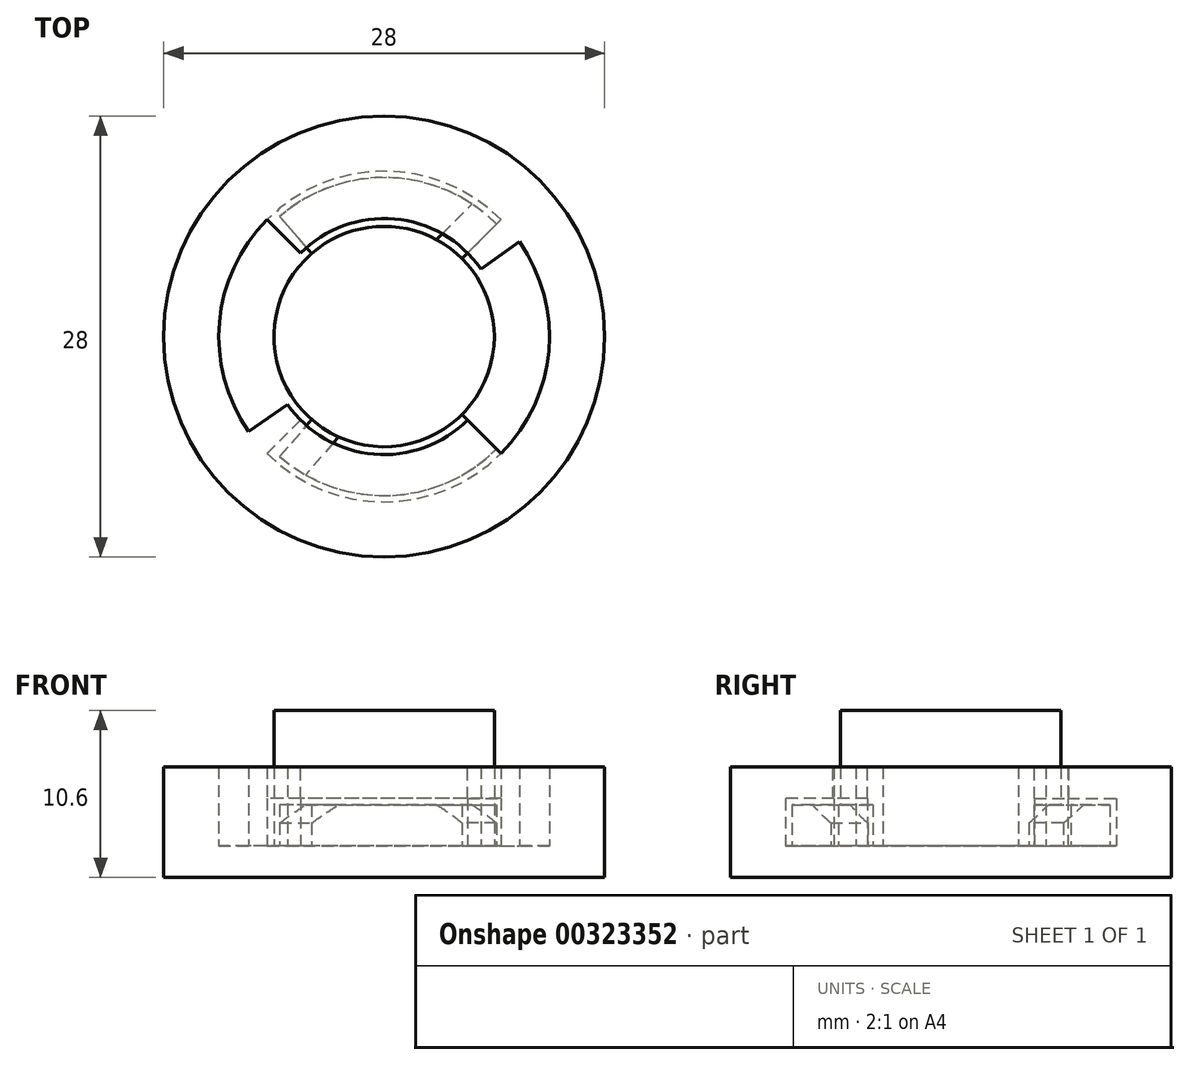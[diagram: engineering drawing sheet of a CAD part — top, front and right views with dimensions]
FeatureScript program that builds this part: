
annotation { "Feature Type Name" : "Feature", "Feature Type Description" : "" }
export const myFeature = defineFeature(function(context is Context, id is Id, definition is map)
    precondition{}
    {
        {
            var Q0;
            Q0=qCreatedBy(makeId("Top.planeOp"),FACE);
            var sketch = newSketch(context, id + "F0", { "sketchPlane" : qUnion([Q0])});
            skCircle(sketch, "E0", {"center": v(0, 0) * mm, "radius": 14 * mm});
            skSolve(sketch);
        }
        {
            var Q0;
            Q0 = qSketchRegion(id + "F0", true);
            extrude(context, id + "F1", {"entities" : qUnion([Q0]), "depth" : 2 * mm, "offsetDistance" : 25 * mm});
        }
        {
            var Q0;
            Q0=makeQuery(id+"F1.opExtrude","CAP_FACE",FACE,{"disambiguationData":[OSD([sQuery(id+"F0.wireOp",EDGE,"E0")])],"isStart":false});
            var sketch = newSketch(context, id + "F2", { "sketchPlane" : qUnion([Q0])});
            skCircle(sketch, "E1", {"center": v(0, 0) * mm, "radius": 14 * mm});
            skCircle(sketch, "E2", {"center": v(0, 0) * mm, "radius": 10.5 * mm});
            skSolve(sketch);
        }
        {
            var Q0;
            Q0 = qSketchRegion(id + "F2", true);
            extrude(context, id + "F3", {"entities" : qUnion([Q0]), "operationType" : NewBodyOperationType.ADD, "depth" : 5 * mm, "offsetDistance" : 25 * mm});
        }
        {
            var Q0;
            Q0=makeQuery(id+"F3.opExtrude","CAP_FACE",FACE,{"disambiguationData":[OSD([sQuery(id+"F2.wireOp",EDGE,"E1"),sQuery(id+"F2.wireOp",EDGE,"E2")])],"isStart":false});
            var sketch = newSketch(context, id + "F4", { "sketchPlane" : qUnion([Q0])});
            skArc(sketch, "E3", {"start": v(-9.9, 9.9) * mm, "mid": v(0, 14) * mm, "end": v(9.9, 9.9) * mm});
            skLineSegment(sketch, "E4", {"start": v(-5.3, 5.3) * mm, "end": v(-9.9, 9.9) * mm});
            skLineSegment(sketch, "E5", {"start": v(5.3, 5.3) * mm, "end": v(9.9, 9.9) * mm});
            skArc(sketch, "E6", {"start": v(-5.3, 5.3) * mm, "mid": v(0, 7.5) * mm, "end": v(5.3, 5.3) * mm});
            skLineSegment(sketch, "E7.MirrorCS", {"start": v(-5.3, -5.3) * mm, "end": v(-9.9, -9.9) * mm});
            skLineSegment(sketch, "E8.MirrorCS", {"start": v(5.3, -5.3) * mm, "end": v(9.9, -9.9) * mm});
            skArc(sketch, "E9.MirrorCS", {"start": v(-5.3, -5.3) * mm, "mid": v(0, -7.5) * mm, "end": v(5.3, -5.3) * mm});
            skArc(sketch, "E10.MirrorCS", {"start": v(-9.9, -9.9) * mm, "mid": v(0, -14) * mm, "end": v(9.9, -9.9) * mm});
            skSolve(sketch);
        }
        {
            var Q0;
            Q0 = qSketchRegion(id + "F4", true);
            extrude(context, id + "F5", {"entities" : qUnion([Q0]), "operationType" : NewBodyOperationType.ADD, "oppositeDirection" : true, "depth" : 2 * mm, "offsetDistance" : 25 * mm});
        }
        {
            var Q0;
            Q0=makeQuery(id+"F1.opExtrude","CAP_FACE",FACE,{"disambiguationData":[OSD([sQuery(id+"F0.wireOp",EDGE,"E0")])],"isStart":false});
            var sketch = newSketch(context, id + "F6", { "sketchPlane" : qUnion([Q0])});
            skLineSegment(sketch, "E11", {"start": v(-11.88, 14.16) * mm, "end": v(11.75, -14) * mm, "construction": true});
            skArc(sketch, "E12", {"start": v(7.42, 7.42) * mm, "mid": v(8.04, 6.75) * mm, "end": v(8.6, 6.02) * mm});
            skArc(sketch, "E13", {"start": v(5.3, 5.3) * mm, "mid": v(5.75, 4.82) * mm, "end": v(6.14, 4.3) * mm});
            skLineSegment(sketch, "E14", {"start": v(6.14, 4.3) * mm, "end": v(8.6, 6.02) * mm});
            skLineSegment(sketch, "E15", {"start": v(5.3, 5.3) * mm, "end": v(7.42, 7.42) * mm});
            skArc(sketch, "E16.MirrorCS", {"start": v(-6.14, -4.3) * mm, "mid": v(-5.75, -4.82) * mm, "end": v(-5.3, -5.3) * mm});
            skArc(sketch, "E17.MirrorCS", {"start": v(-8.6, -6.02) * mm, "mid": v(-8.04, -6.75) * mm, "end": v(-7.42, -7.42) * mm});
            skLineSegment(sketch, "E18.MirrorCS", {"start": v(-5.3, -5.3) * mm, "end": v(-7.42, -7.42) * mm});
            skLineSegment(sketch, "E19.MirrorCS", {"start": v(-6.14, -4.3) * mm, "end": v(-8.6, -6.02) * mm});
            skSolve(sketch);
        }
        {
            var Q0;
            Q0 = qSketchRegion(id + "F6", true);
            var Q1;
            Q1=makeQuery(id+"F5.boolean.opBoolean","MERGE",FACE,{"derivedFrom":[makeQuery(id+"F3.opExtrude","CAP_FACE",FACE,{"disambiguationData":[OSD([sQuery(id+"F2.wireOp",EDGE,"E1"),sQuery(id+"F2.wireOp",EDGE,"E2")])],"isStart":false}),makeQuery(id+"F5.opExtrude","CAP_FACE",FACE,{"disambiguationData":[OSD([sQuery(id+"F4.wireOp",EDGE,"E3"),sQuery(id+"F4.wireOp",EDGE,"E4"),sQuery(id+"F4.wireOp",EDGE,"E5"),sQuery(id+"F4.wireOp",EDGE,"E6")])],"isStart":true}),makeQuery(id+"F5.opExtrude","CAP_FACE",FACE,{"disambiguationData":[OSD([sQuery(id+"F4.wireOp",EDGE,"E7.MirrorCS"),sQuery(id+"F4.wireOp",EDGE,"E8.MirrorCS"),sQuery(id+"F4.wireOp",EDGE,"E9.MirrorCS"),sQuery(id+"F4.wireOp",EDGE,"E10.MirrorCS")])],"isStart":true})]});
            extrude(context, id + "F7", {"entities" : qUnion([Q0]), "operationType" : NewBodyOperationType.ADD, "endBound" : BoundingType.UP_TO_SURFACE, "depth" : 25 * mm, "endBoundEntityFace" : qUnion([Q1]), "offsetDistance" : 25 * mm});
        }
        {
            var Q0;
            Q0=makeQuery(id+"F1.opExtrude","CAP_FACE",FACE,{"disambiguationData":[OSD([sQuery(id+"F0.wireOp",EDGE,"E0")])],"isStart":false});
            var sketch = newSketch(context, id + "F8", { "sketchPlane" : qUnion([Q0])});
            skArc(sketch, "E20", {"start": v(-6.63, 7.62) * mm, "mid": v(0.35, 10.1) * mm, "end": v(7.14, 7.14) * mm});
            skLineSegment(sketch, "E21", {"start": v(-4.6, 5.28) * mm, "end": v(-6.63, 7.62) * mm});
            skLineSegment(sketch, "E22", {"start": v(4.95, 4.95) * mm, "end": v(7.14, 7.14) * mm});
            skLineSegment(sketch, "E23.MirrorCS", {"start": v(4.95, -4.95) * mm, "end": v(7.14, -7.14) * mm});
            skArc(sketch, "E24.MirrorCS", {"start": v(-6.63, -7.62) * mm, "mid": v(0.35, -10.1) * mm, "end": v(7.14, -7.14) * mm});
            skLineSegment(sketch, "E25.MirrorCS", {"start": v(-4.6, -5.28) * mm, "end": v(-6.63, -7.62) * mm});
            skArc(sketch, "E26", {"start": v(-4.6, 5.28) * mm, "mid": v(-7, 0) * mm, "end": v(-4.6, -5.28) * mm});
            skArc(sketch, "E27.trimOffspring", {"start": v(4.95, -4.95) * mm, "mid": v(7, 0) * mm, "end": v(4.95, 4.95) * mm});
            skSolve(sketch);
        }
        {
            var Q0;
            Q0 = qSketchRegion(id + "F8", true);
            extrude(context, id + "F9", {"entities" : qUnion([Q0]), "depth" : 2.6 * mm, "offsetDistance" : 25 * mm});
        }
        {
            var Q0;
            Q0=makeQuery(id+"F9.opExtrude","CAP_FACE",FACE,{"disambiguationData":[OSD([sQuery(id+"F8.wireOp",EDGE,"E20"),sQuery(id+"F8.wireOp",EDGE,"E21"),sQuery(id+"F8.wireOp",EDGE,"E22"),sQuery(id+"F8.wireOp",EDGE,"E23.MirrorCS"),sQuery(id+"F8.wireOp",EDGE,"E24.MirrorCS"),sQuery(id+"F8.wireOp",EDGE,"E25.MirrorCS"),sQuery(id+"F8.wireOp",EDGE,"E26"),sQuery(id+"F8.wireOp",EDGE,"E27.trimOffspring")])],"isStart":false});
            var sketch = newSketch(context, id + "F10", { "sketchPlane" : qUnion([Q0])});
            skCircle(sketch, "E28", {"center": v(0, 0) * mm, "radius": 7 * mm});
            skSolve(sketch);
        }
        {
            var Q0;
            Q0 = qSketchRegion(id + "F10", true);
            extrude(context, id + "F11", {"entities" : qUnion([Q0]), "operationType" : NewBodyOperationType.ADD, "depth" : 6 * mm, "offsetDistance" : 25 * mm});
        }
        {
            var Q0;
            Q0=makeQuery(id+"F9.opExtrude","CAP_EDGE",EDGE,{"disambiguationData":[OSD([sQuery(id+"F8.wireOp",EDGE,"E22")])],"isStart":false});
            var Q1;
            Q1=makeQuery(id+"F9.opExtrude","CAP_EDGE",EDGE,{"disambiguationData":[OSD([sQuery(id+"F8.wireOp",EDGE,"E25.MirrorCS")])],"isStart":false});
            chamfer(context, id + "F12", {"entities" : qUnion([Q0, Q1]), "chamferType" : ChamferType.OFFSET_ANGLE, "width" : 2 * mm, "oppositeDirection" : false, "angle" : 30 * degree, "tangentPropagation" : true});
        }
    });
